# Revit family: Hand_Dryer-Bradley_Corp-Aerix-2922
name_source: partatom
category: Electrical Fixtures
revit_build: Autodesk Revit Architecture 2012 (Build: 20110916_2132(x64)
units: mm (PartAtom-declared; Revit-internal decimal feet)

## types (4) — shared parameters
Actuation = as Specified
Air Output = 265 MPH at 100 CFM
Air Temperature = 41 degrees above ambient room temperature
Assembly Code = C1030210
Automatic = Yes
Drying Time = 10 seconds
Frame Finish = Metal - Bradley Corporation - Brushed Stainless Steel
Frequency = 60 Hz
Hardware Finish = Metal - Bradley Corp - Chrome
Keynote = 10810
MEP Amperage = 10 A
MEP Apparent Power = 1200 VA
Manufacturer = Bradley Corporation
Revision = 1.0
Sound Pressure = 73 dB on High ; 68 dB on Medium ; 64 dB on Low
URL = http://www.bradleycorp.com
Unit Depth = 7.6 "
Unit Length = 12.5 "
Unit Width = 9.3 "
Voltage_MEP = 120 V
zero-valued in all types: Expected Lifespan (Years), Maintenance Schedule (Months), Warranty Duration (Years)

## per-type parameters (varying)
| type | ADA Compliant | Cover Material | Default Elevation | Description | Model | Recessed | Standards Conformance | Surface Finish | Unit Weight | recessdryer | recessvoid |
| Stainless Steel-Satin Finish - Recessed with Kit | Yes | Metal - Bradley Corporation - Stainless Steel | 0 " | Bradley Aerix+ Automatic Hand Dryer with Recess Kit - 110-120V - 400-1200W -  78-100CFM | Aerix+ 2922-2873 | Yes | cULus   ;   CE   ;   TUV-GS   ;   IP24 Housing   ;   GreenSpec   ;   ADA | Metal - Bradley Corporation - Stainless Steel | 11.6 | 3.8 " | 3.9 " |
| White Aluminum - Recessed with Kit | Yes | Metal - Bradley Corporation - Aluminum | 48 " | Bradley Aerix+ Automatic Hand Dryer with Recess Kit - 110-120V - 400-1200W -  78-100CFM | Aerix+ 2922-2873 | Yes | cULus   ;   CE   ;   TUV-GS   ;   IP24 Housing   ;   GreenSpec   ;   ADA | Metal - Bradley Corporation - White | 11.6 | 3.8 " | 3.9 " |
| Stainless Steel-Satin Finish - Surface Mounted | No | Metal - Bradley Corporation - Stainless Steel | 48 " | Bradley Aerix+ Automatic Hand Dryer - 110-120V - 400-1200W -  78-100CFM | Aerix+ 2922-2874 | No | cULus   ;   CE   ;   TUV-GS   ;   IP24 Housing   ;   GreenSpec | Metal - Bradley Corporation - Stainless Steel | 14.2 | 0 " | 0 " |
| White Aluminum - Surface Mounted | No | Metal - Bradley Corporation - Aluminum | 48 " | Bradley Aerix+ Automatic Hand Dryer - 110-120V - 400-1200W -  78-100CFM | Aerix+ 2922-2873 | No | cULus   ;   CE   ;   TUV-GS   ;   IP24 Housing   ;   GreenSpec | Metal - Bradley Corporation - White | 11.6 | 0 " | 0 " |

## geometry (parser evidence)
native form markers: Blend x6, Sweep x5
no freeform markers — native parametric forms only
